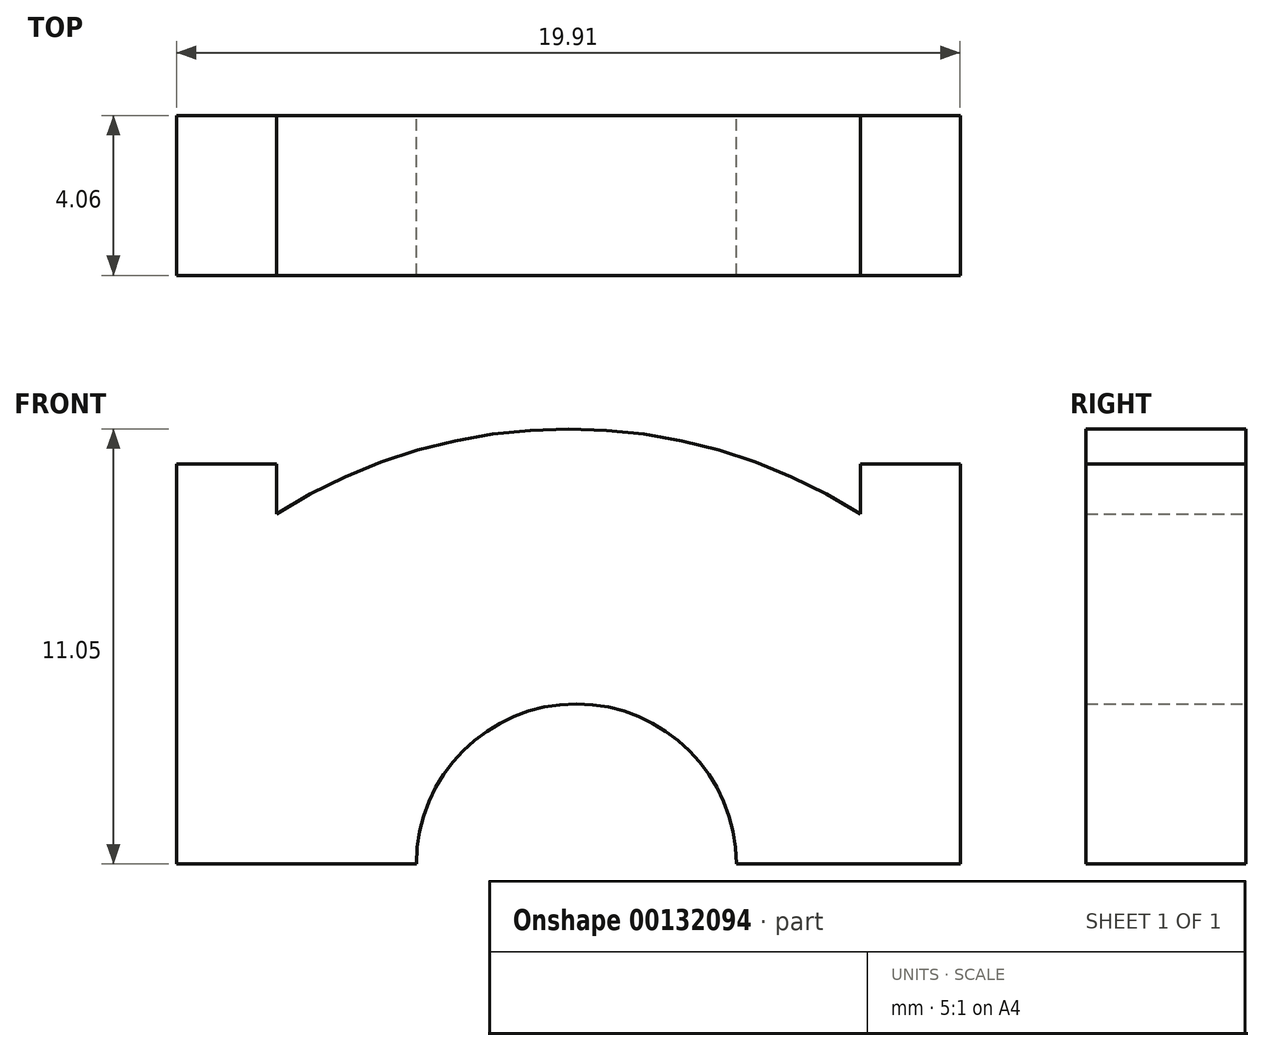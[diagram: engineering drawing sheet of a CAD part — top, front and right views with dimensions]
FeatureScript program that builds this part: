
annotation { "Feature Type Name" : "Feature", "Feature Type Description" : "" }
export const myFeature = defineFeature(function(context is Context, id is Id, definition is map)
    precondition{}
    {
        {
            var Q0;
            Q0=qCreatedBy(makeId("Front.planeOp"),FACE);
            var sketch = newSketch(context, id + "F0", { "sketchPlane" : qUnion([Q0])});
            skArc(sketch, "E0", {"start": v(20.32, 0) * mm, "mid": v(0, 20.32) * mm, "end": v(-20.32, 0) * mm});
            skLineSegment(sketch, "E1", {"start": v(-20.32, 0) * mm, "end": v(-50.8, 0) * mm});
            skLineSegment(sketch, "E2", {"start": v(20.32, 0) * mm, "end": v(48.77, 0) * mm});
            skLineSegment(sketch, "E3", {"start": v(-50.8, 0) * mm, "end": v(-50.8, 50.8) * mm});
            skLineSegment(sketch, "E4", {"start": v(48.77, 0) * mm, "end": v(48.77, 50.8) * mm});
            skLineSegment(sketch, "E5", {"start": v(-50.8, 50.8) * mm, "end": v(-38.1, 50.8) * mm});
            skLineSegment(sketch, "E6", {"start": v(-38.1, 50.8) * mm, "end": v(-38.1, 44.45) * mm});
            skLineSegment(sketch, "E7", {"start": v(48.77, 50.8) * mm, "end": v(36.07, 50.8) * mm});
            skLineSegment(sketch, "E8", {"start": v(36.07, 50.8) * mm, "end": v(36.07, 44.45) * mm});
            skArc(sketch, "E9", {"start": v(36.07, 44.45) * mm, "mid": v(-1.01, 55.25) * mm, "end": v(-38.1, 44.45) * mm});
            skSolve(sketch);
        }
        {
            var Q0;
            Q0=makeQuery(id+"F0.imprint","IMPRINT",FACE,{"disambiguationData":[TD([[makeQuery(id+"F0.imprint","IMPRINT",EDGE,{"derivedFrom":sQuery(id+"F0.wireOp",EDGE,"E0")}),-1.0]])]});
            extrude(context, id + "F1", {"entities" : qUnion([Q0]), "depth" : 20.32 * mm});
        }
        {
            var Q0;
            Q0=makeQuery(id+"F1.opExtrude","SWEPT_BODY",BODY,{"disambiguationData":[OSD([sQuery(id+"F0.wireOp",EDGE,"E0"),sQuery(id+"F0.wireOp",EDGE,"E1"),sQuery(id+"F0.wireOp",EDGE,"E2"),sQuery(id+"F0.wireOp",EDGE,"E3"),sQuery(id+"F0.wireOp",EDGE,"E4"),sQuery(id+"F0.wireOp",EDGE,"E5"),sQuery(id+"F0.wireOp",EDGE,"E6"),sQuery(id+"F0.wireOp",EDGE,"E7"),sQuery(id+"F0.wireOp",EDGE,"E8"),sQuery(id+"F0.wireOp",EDGE,"E9")])]});
            var Q1;
            Q1=qCreatedBy(makeId("Origin.pointOp"),VERTEX);
            transform(context, id + "F2", {"entities" : qUnion([Q0]), "transformType" : TransformType.SCALE_UNIFORMLY, "scale" : .2, "scalePoint" : qUnion([Q1]), "makeCopy" : false});
        }
    });
